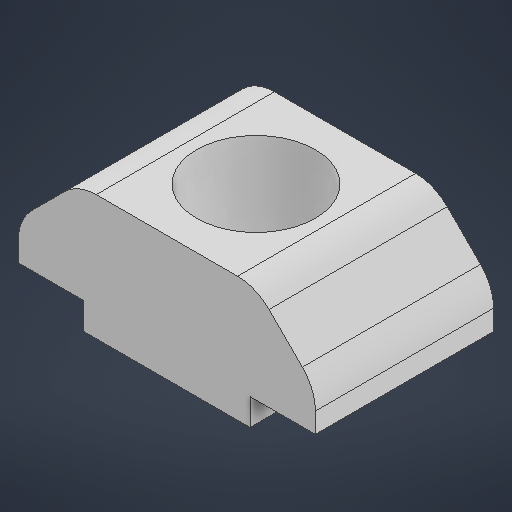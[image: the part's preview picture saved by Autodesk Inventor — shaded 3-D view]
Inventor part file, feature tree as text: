
AUTODESK INVENTOR PART (.ipt)
format: ipt  version: 2025.1 (Build 291241000, 241)  size: 209,408 bytes
history: native  units: mm
features: extrude x2, sketch x1, chamfer x1, fillet x1
ambient origin geometry x8: Origin, YZ Plane, XZ Plane, XY Plane, X Axis, Y Axis, Z Axis, Center Point
bodies: Solid1 (feature_tree)
feature tree (5):
  sketch  "Sketch1"  dims[d0=10.0mm d1=6.0mm d2=4.2mm d3=0.0mm d5=5.6mm d6=0.9mm d7=0.0mm d8=2.0mm d9=2.0mm d10=45.0deg d11=4.0mm d12=1.5mm]
  extrude  "Extrusion1"  Depth=6.0mm
  extrude  "Extrusion2"  Depth=4.2mm TaperAngle=0.0deg
  chamfer  "Chamfer1"  Distance=5.6mm
  fillet  "Fillet1"  Radius=0.9mm
